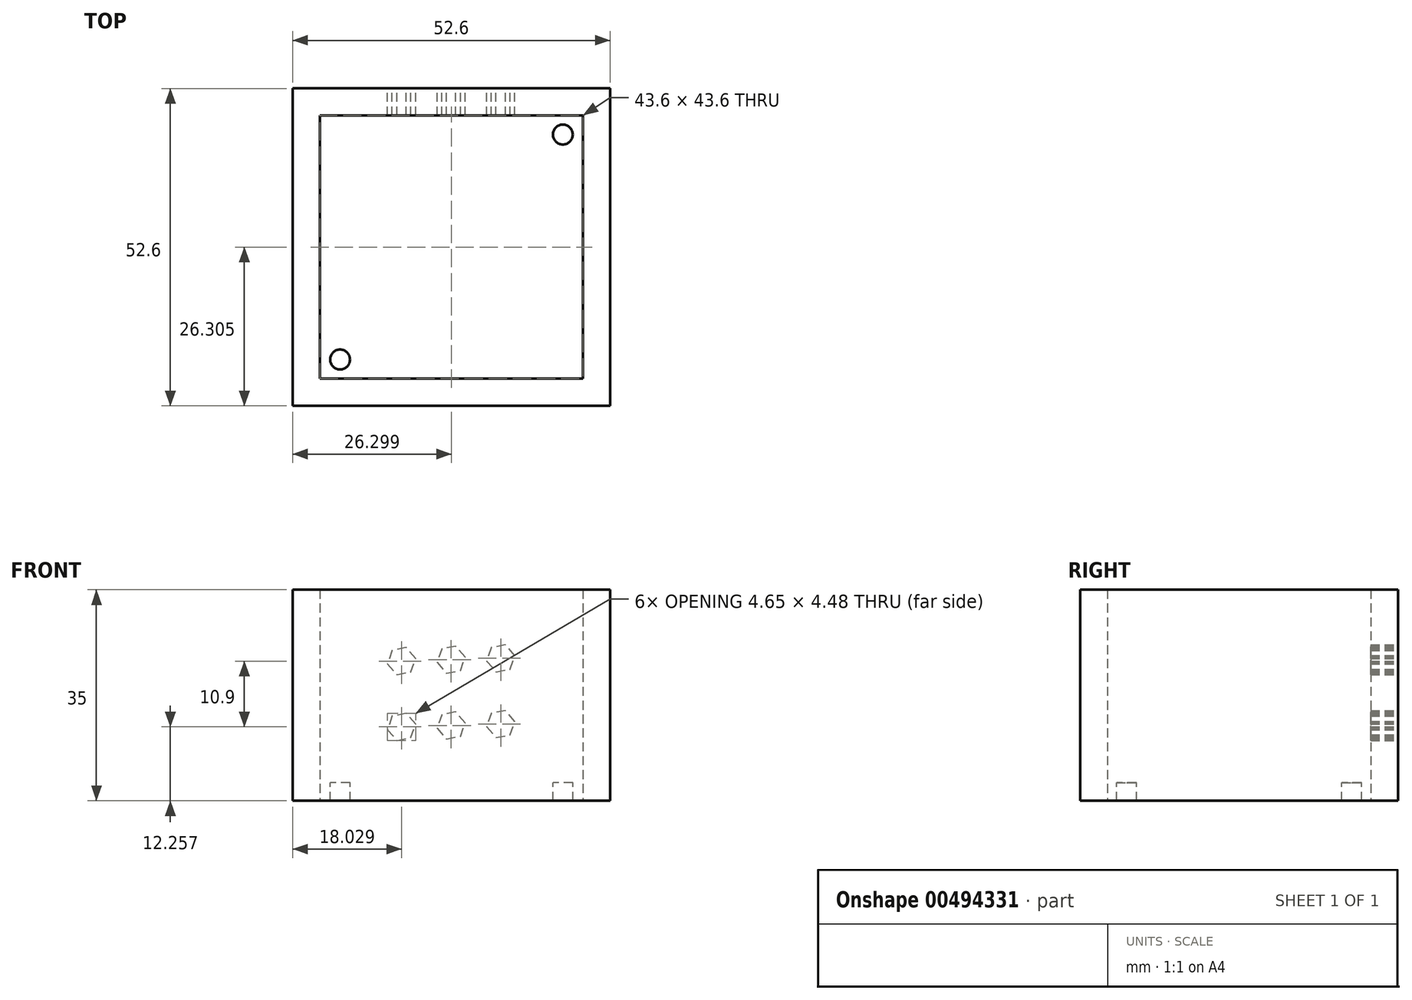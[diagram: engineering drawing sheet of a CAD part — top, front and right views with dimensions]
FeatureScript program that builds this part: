
annotation { "Feature Type Name" : "Feature", "Feature Type Description" : "" }
export const myFeature = defineFeature(function(context is Context, id is Id, definition is map)
    precondition{}
    {
        {
            var Q0;
            Q0=qCreatedBy(makeId("Top.planeOp"),FACE);
            var sketch = newSketch(context, id + "F0", { "sketchPlane" : qUnion([Q0])});
            skLineSegment(sketch, "E0.bottom", {"start": v(-23.4, 22.41) * mm, "end": v(20.2, 22.41) * mm});
            skLineSegment(sketch, "E0.top", {"start": v(-23.4, -21.19) * mm, "end": v(20.2, -21.19) * mm});
            skLineSegment(sketch, "E0.left", {"start": v(-23.4, 22.41) * mm, "end": v(-23.4, -21.19) * mm});
            skLineSegment(sketch, "E0.right", {"start": v(20.2, 22.41) * mm, "end": v(20.2, -21.19) * mm});
            skSolve(sketch);
        }
        {
            var Q0;
            Q0=qCreatedBy(makeId("Top.planeOp"),FACE);
            var sketch = newSketch(context, id + "F1", { "sketchPlane" : qUnion([Q0])});
            skLineSegment(sketch, "E1.0", {"start": v(-23.4, 26.91) * mm, "end": v(20.2, 26.91) * mm});
            skLineSegment(sketch, "E2.0", {"start": v(-27.9, 22.41) * mm, "end": v(-27.9, -21.19) * mm});
            skLineSegment(sketch, "E3.0", {"start": v(-23.4, -25.69) * mm, "end": v(20.2, -25.69) * mm});
            skLineSegment(sketch, "E4.0", {"start": v(24.7, 22.41) * mm, "end": v(24.7, -21.19) * mm});
            skLineSegment(sketch, "E5", {"start": v(-27.9, 22.41) * mm, "end": v(-27.9, 26.91) * mm});
            skLineSegment(sketch, "E6", {"start": v(-27.9, 26.91) * mm, "end": v(-23.4, 26.91) * mm});
            skLineSegment(sketch, "E7", {"start": v(20.2, 26.91) * mm, "end": v(24.7, 26.91) * mm});
            skLineSegment(sketch, "E8", {"start": v(24.7, 26.91) * mm, "end": v(24.7, 22.41) * mm});
            skLineSegment(sketch, "E9", {"start": v(24.7, -21.19) * mm, "end": v(24.7, -25.69) * mm});
            skLineSegment(sketch, "E10", {"start": v(24.7, -25.69) * mm, "end": v(20.2, -25.69) * mm});
            skLineSegment(sketch, "E11", {"start": v(-27.9, -21.19) * mm, "end": v(-27.9, -25.69) * mm});
            skLineSegment(sketch, "E12", {"start": v(-27.9, -25.69) * mm, "end": v(-23.4, -25.69) * mm});
            skLineSegment(sketch, "E13.0", {"start": v(20.2, 22.41) * mm, "end": v(20.2, -21.19) * mm});
            skLineSegment(sketch, "E13.1", {"start": v(-23.4, 22.41) * mm, "end": v(20.2, 22.41) * mm});
            skLineSegment(sketch, "E13.2", {"start": v(-23.4, 22.41) * mm, "end": v(-23.4, -21.19) * mm});
            skLineSegment(sketch, "E13.3", {"start": v(-23.4, -21.19) * mm, "end": v(20.2, -21.19) * mm});
            skSolve(sketch);
        }
        {
            var Q0;
            Q0=makeQuery(id+"F0.imprint","IMPRINT",FACE,{"disambiguationData":[TD([[makeQuery(id+"F0.imprint","IMPRINT",EDGE,{"derivedFrom":sQuery(id+"F0.wireOp",EDGE,"E0.bottom")}),-1.0]])]});
            extrude(context, id + "F2", {"entities" : qUnion([Q0]), "depth" : 3 * mm});
        }
        {
            var Q0;
            Q0=makeQuery(id+"F2.opExtrude","CAP_FACE",FACE,{"disambiguationData":[OSD([sQuery(id+"F0.wireOp",EDGE,"E0.bottom"),sQuery(id+"F0.wireOp",EDGE,"E0.top"),sQuery(id+"F0.wireOp",EDGE,"E0.left"),sQuery(id+"F0.wireOp",EDGE,"E0.right")])],"isStart":false});
            var sketch = newSketch(context, id + "F3", { "sketchPlane" : qUnion([Q0])});
            skCircle(sketch, "E14", {"center": v(-20.05, 19.26) * mm, "radius": 1.65 * mm});
            skCircle(sketch, "E15.MirrorC", {"center": v(16.85, 19.26) * mm, "radius": 1.65 * mm});
            skCircle(sketch, "E16.MirrorC", {"center": v(16.85, -18.04) * mm, "radius": 1.65 * mm});
            skCircle(sketch, "E17.MirrorC", {"center": v(-20.05, -18.04) * mm, "radius": 1.65 * mm});
            skSolve(sketch);
        }
        {
            var Q0;
            Q0=makeQuery(id+"F3.imprint","IMPRINT",FACE,{"disambiguationData":[TD([[makeQuery(id+"F3.imprint","IMPRINT",EDGE,{"derivedFrom":sQuery(id+"F3.wireOp",EDGE,"E14")}),1.0]])]});
            var Q1;
            Q1=makeQuery(id+"F3.imprint","IMPRINT",FACE,{"disambiguationData":[TD([[makeQuery(id+"F3.imprint","IMPRINT",EDGE,{"derivedFrom":sQuery(id+"F3.wireOp",EDGE,"E15.MirrorC")}),-1.0]])]});
            var Q2;
            Q2=makeQuery(id+"F3.imprint","IMPRINT",FACE,{"disambiguationData":[TD([[makeQuery(id+"F3.imprint","IMPRINT",EDGE,{"derivedFrom":sQuery(id+"F3.wireOp",EDGE,"E16.MirrorC")}),1.0]])]});
            var Q3;
            Q3=makeQuery(id+"F3.imprint","IMPRINT",FACE,{"disambiguationData":[TD([[makeQuery(id+"F3.imprint","IMPRINT",EDGE,{"derivedFrom":sQuery(id+"F3.wireOp",EDGE,"E17.MirrorC")}),-1.0]])]});
            extrude(context, id + "F4", {"entities" : qUnion([Q0, Q1, Q2, Q3]), "operationType" : NewBodyOperationType.REMOVE, "oppositeDirection" : true, "depth" : 25 * mm});
        }
        {
            var Q0;
            Q0=makeQuery(id+"F1.imprint","IMPRINT",FACE,{"disambiguationData":[TD([[makeQuery(id+"F1.imprint","IMPRINT",EDGE,{"derivedFrom":sQuery(id+"F1.wireOp",EDGE,"E1.0")}),-1.0]])]});
            extrude(context, id + "F5", {"entities" : qUnion([Q0]), "operationType" : NewBodyOperationType.ADD, "depth" : 35 * mm});
        }
        {
            var Q0;
            Q0=makeQuery(id+"F5.opExtrude","SWEPT_FACE",FACE,{"disambiguationData":[OSD([sQuery(id+"F1.wireOp",EDGE,"E1.0"),sQuery(id+"F1.wireOp",EDGE,"E6"),sQuery(id+"F1.wireOp",EDGE,"E7")])]});
            var sketch = newSketch(context, id + "F6", { "sketchPlane" : qUnion([Q0])});
            skCircle(sketch, "E18.cCircle", {"center": v(-6.56, 23.62) * mm, "radius": 2.05 * mm, "construction": true});
            skLineSegment(sketch, "E18.0", {"start": v(-4.23, 23.16) * mm, "end": v(-5.8, 21.38) * mm});
            skLineSegment(sketch, "E18.1", {"start": v(-5.8, 21.38) * mm, "end": v(-8.12, 21.83) * mm});
            skLineSegment(sketch, "E18.2", {"start": v(-8.12, 21.83) * mm, "end": v(-8.88, 24.07) * mm});
            skLineSegment(sketch, "E18.3", {"start": v(-8.88, 24.07) * mm, "end": v(-7.33, 25.86) * mm});
            skLineSegment(sketch, "E18.4", {"start": v(-7.33, 25.86) * mm, "end": v(-5, 25.4) * mm});
            skLineSegment(sketch, "E18.5", {"start": v(-5, 25.4) * mm, "end": v(-4.23, 23.16) * mm});
            skPoint(sketch, "E18.0.midPoint", {"position": v(-5.01, 22.27) * mm});
            skLineSegment(sketch, "E19.direction1", {"start": v(-6.56, 23.62) * mm, "end": v(1.34, 23.62) * mm, "construction": true});
            skLineSegment(sketch, "E20.0.1.0", {"start": v(-5.8, 10.48) * mm, "end": v(-8.12, 10.93) * mm});
            skLineSegment(sketch, "E20.0.1.1", {"start": v(-8.12, 10.93) * mm, "end": v(-8.88, 13.17) * mm});
            skLineSegment(sketch, "E20.0.1.2", {"start": v(-4.23, 12.26) * mm, "end": v(-5.8, 10.48) * mm});
            skCircle(sketch, "E20.0.1.3", {"center": v(-6.56, 12.72) * mm, "radius": 2.05 * mm, "construction": true});
            skPoint(sketch, "E20.0.1.4", {"position": v(-5.01, 11.37) * mm});
            skLineSegment(sketch, "E20.0.1.5", {"start": v(-5, 14.5) * mm, "end": v(-4.23, 12.26) * mm});
            skLineSegment(sketch, "E20.0.1.6", {"start": v(-8.88, 13.17) * mm, "end": v(-7.33, 14.96) * mm});
            skLineSegment(sketch, "E20.0.1.7", {"start": v(-7.33, 14.96) * mm, "end": v(-5, 14.5) * mm});
            skLineSegment(sketch, "E20.1.0.0", {"start": v(2.42, 21.15) * mm, "end": v(0.1, 21.6) * mm});
            skLineSegment(sketch, "E20.1.0.1", {"start": v(0.1, 21.6) * mm, "end": v(-0.67, 23.84) * mm});
            skLineSegment(sketch, "E20.1.0.2", {"start": v(3.98, 22.93) * mm, "end": v(2.42, 21.15) * mm});
            skCircle(sketch, "E20.1.0.3", {"center": v(1.66, 23.39) * mm, "radius": 2.05 * mm, "construction": true});
            skPoint(sketch, "E20.1.0.4", {"position": v(3.2, 22.04) * mm});
            skLineSegment(sketch, "E20.1.0.5", {"start": v(3.21, 25.17) * mm, "end": v(3.98, 22.93) * mm});
            skLineSegment(sketch, "E20.1.0.6", {"start": v(-0.67, 23.84) * mm, "end": v(0.89, 25.63) * mm});
            skLineSegment(sketch, "E20.1.0.7", {"start": v(0.89, 25.63) * mm, "end": v(3.21, 25.17) * mm});
            skLineSegment(sketch, "E20.1.1.0", {"start": v(2.42, 10.25) * mm, "end": v(0.1, 10.7) * mm});
            skLineSegment(sketch, "E20.1.1.1", {"start": v(0.1, 10.7) * mm, "end": v(-0.67, 12.94) * mm});
            skLineSegment(sketch, "E20.1.1.2", {"start": v(3.98, 12.03) * mm, "end": v(2.42, 10.25) * mm});
            skCircle(sketch, "E20.1.1.3", {"center": v(1.66, 12.49) * mm, "radius": 2.05 * mm, "construction": true});
            skPoint(sketch, "E20.1.1.4", {"position": v(3.2, 11.14) * mm});
            skLineSegment(sketch, "E20.1.1.5", {"start": v(3.21, 14.27) * mm, "end": v(3.98, 12.03) * mm});
            skLineSegment(sketch, "E20.1.1.6", {"start": v(-0.67, 12.94) * mm, "end": v(0.89, 14.73) * mm});
            skLineSegment(sketch, "E20.1.1.7", {"start": v(0.89, 14.73) * mm, "end": v(3.21, 14.27) * mm});
            skLineSegment(sketch, "E20.2.0.0", {"start": v(10.64, 20.92) * mm, "end": v(8.32, 21.37) * mm});
            skLineSegment(sketch, "E20.2.0.1", {"start": v(8.32, 21.37) * mm, "end": v(7.55, 23.61) * mm});
            skLineSegment(sketch, "E20.2.0.2", {"start": v(12.2, 22.7) * mm, "end": v(10.64, 20.92) * mm});
            skCircle(sketch, "E20.2.0.3", {"center": v(9.87, 23.16) * mm, "radius": 2.05 * mm, "construction": true});
            skPoint(sketch, "E20.2.0.4", {"position": v(11.42, 21.8) * mm});
            skLineSegment(sketch, "E20.2.0.5", {"start": v(11.43, 24.94) * mm, "end": v(12.2, 22.7) * mm});
            skLineSegment(sketch, "E20.2.0.6", {"start": v(7.55, 23.61) * mm, "end": v(9.1, 25.4) * mm});
            skLineSegment(sketch, "E20.2.0.7", {"start": v(9.1, 25.4) * mm, "end": v(11.43, 24.94) * mm});
            skLineSegment(sketch, "E20.2.1.0", {"start": v(10.64, 10.02) * mm, "end": v(8.32, 10.47) * mm});
            skLineSegment(sketch, "E20.2.1.1", {"start": v(8.32, 10.47) * mm, "end": v(7.55, 12.71) * mm});
            skLineSegment(sketch, "E20.2.1.2", {"start": v(12.2, 11.8) * mm, "end": v(10.64, 10.02) * mm});
            skCircle(sketch, "E20.2.1.3", {"center": v(9.87, 12.26) * mm, "radius": 2.05 * mm, "construction": true});
            skPoint(sketch, "E20.2.1.4", {"position": v(11.42, 10.9) * mm});
            skLineSegment(sketch, "E20.2.1.5", {"start": v(11.43, 14.04) * mm, "end": v(12.2, 11.8) * mm});
            skLineSegment(sketch, "E20.2.1.6", {"start": v(7.55, 12.71) * mm, "end": v(9.1, 14.5) * mm});
            skLineSegment(sketch, "E20.2.1.7", {"start": v(9.1, 14.5) * mm, "end": v(11.43, 14.04) * mm});
            skLineSegment(sketch, "E20.direction1", {"start": v(-8.12, 21.83) * mm, "end": v(0.1, 21.6) * mm, "construction": true});
            skLineSegment(sketch, "E20.direction2", {"start": v(-8.12, 21.83) * mm, "end": v(-8.12, 10.93) * mm, "construction": true});
            skSolve(sketch);
        }
        {
            var Q0;
            Q0 = qSketchRegion(id + "F6", true);
            extrude(context, id + "F7", {"entities" : qUnion([Q0]), "operationType" : NewBodyOperationType.REMOVE, "oppositeDirection" : true, "depth" : 25 * mm});
        }
    });
